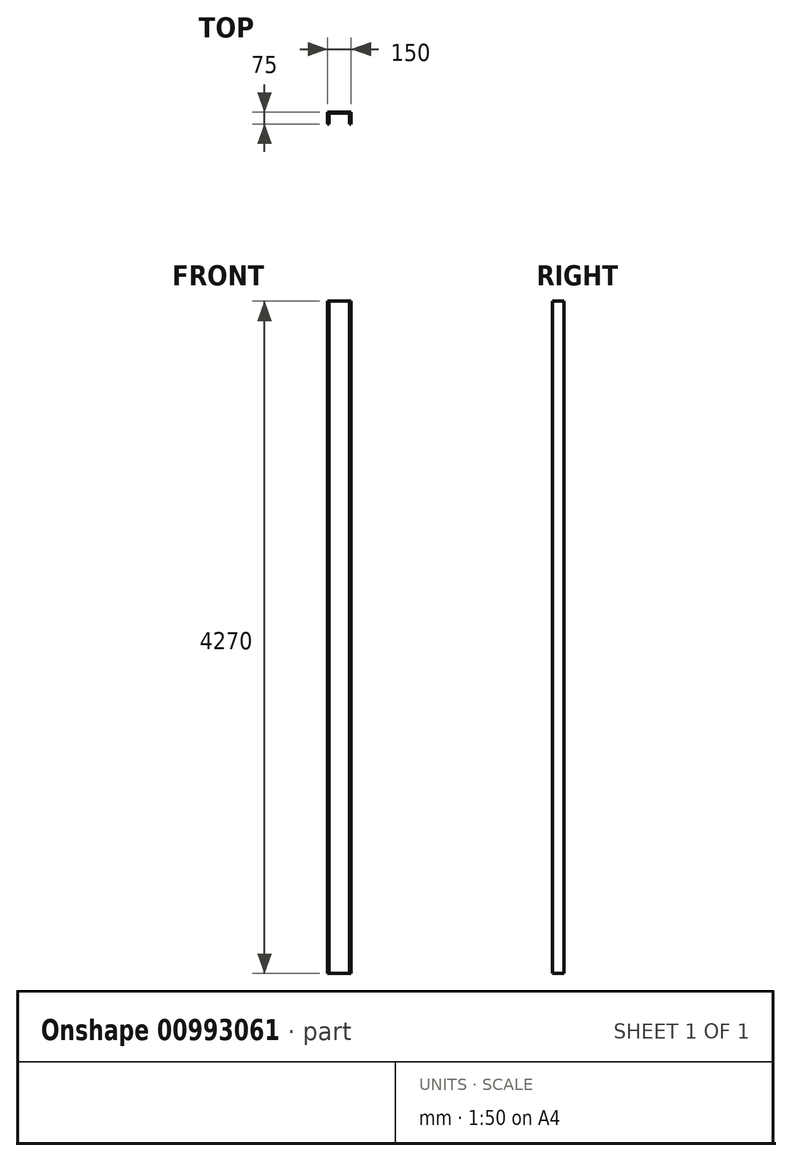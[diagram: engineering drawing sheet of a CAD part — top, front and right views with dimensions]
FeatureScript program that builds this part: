
annotation { "Feature Type Name" : "Feature", "Feature Type Description" : "" }
export const myFeature = defineFeature(function(context is Context, id is Id, definition is map)
    precondition{}
    {
        {
            var Q0;
            Q0=qCreatedBy(makeId("Top.planeOp"),FACE);
            var sketch = newSketch(context, id + "F0", { "sketchPlane" : qUnion([Q0])});
            skLineSegment(sketch, "E0", {"start": v(0, 0) * mm, "end": v(0, 75) * mm});
            skLineSegment(sketch, "E1", {"start": v(0, 75) * mm, "end": v(150, 75) * mm});
            skLineSegment(sketch, "E2", {"start": v(150, 75) * mm, "end": v(150, 0) * mm});
            skLineSegment(sketch, "E3", {"start": v(150, 0) * mm, "end": v(140, 0) * mm});
            skLineSegment(sketch, "E4", {"start": v(140, 0) * mm, "end": v(140, 69.5) * mm});
            skLineSegment(sketch, "E5", {"start": v(140, 69.5) * mm, "end": v(10, 69.5) * mm});
            skLineSegment(sketch, "E6", {"start": v(10, 69.5) * mm, "end": v(10, 0) * mm});
            skLineSegment(sketch, "E7", {"start": v(10, 0) * mm, "end": v(0, 0) * mm});
            skSolve(sketch);
        }
        {
            var Q0;
            Q0=makeQuery(id+"F0.imprint","IMPRINT",FACE,{"disambiguationData":[TD([[makeQuery(id+"F0.imprint","IMPRINT",EDGE,{"derivedFrom":sQuery(id+"F0.wireOp",EDGE,"E0")}),-1.0]])]});
            extrude(context, id + "F1", {"entities" : qUnion([Q0]), "depth" : 4270 * mm, "offsetDistance" : 25 * mm});
        }
    });
